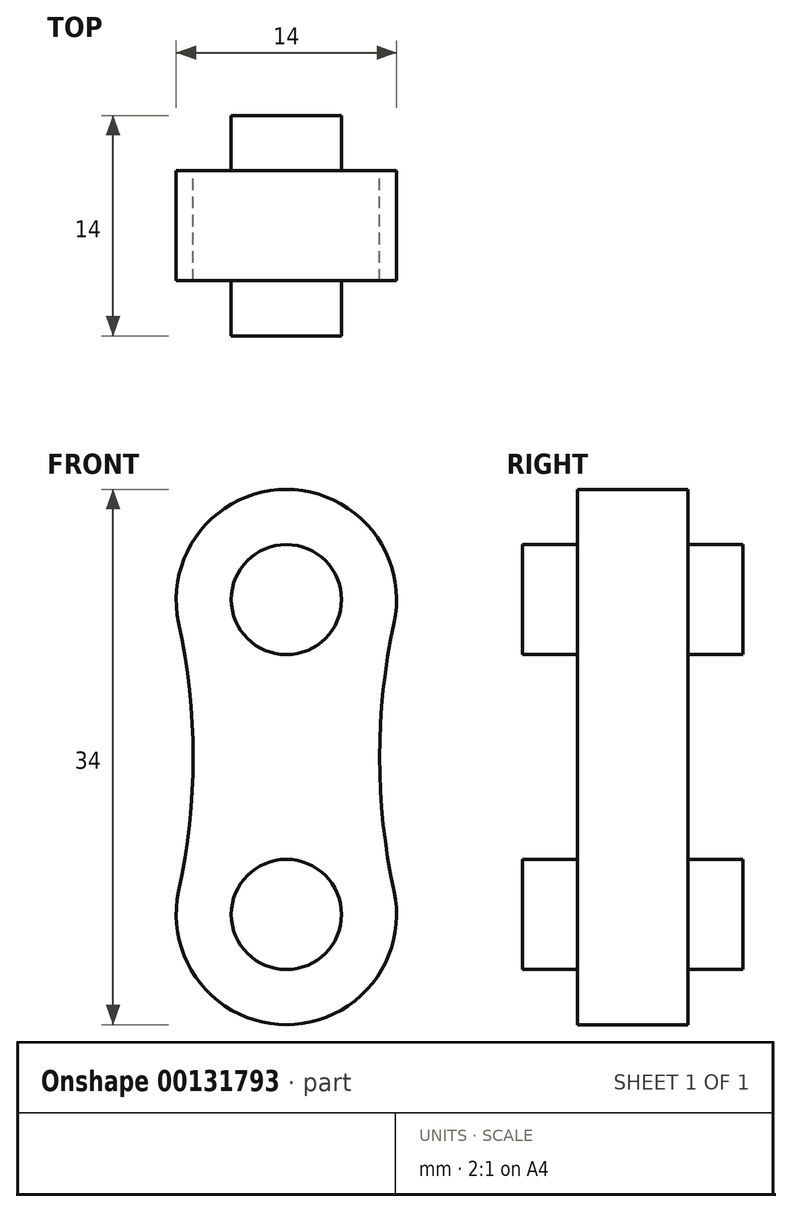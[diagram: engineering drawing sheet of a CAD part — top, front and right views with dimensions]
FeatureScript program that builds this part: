
annotation { "Feature Type Name" : "Feature", "Feature Type Description" : "" }
export const myFeature = defineFeature(function(context is Context, id is Id, definition is map)
    precondition{}
    {
        {
            var Q0;
            Q0=qCreatedBy(makeId("Front.planeOp"),FACE);
            var sketch = newSketch(context, id + "F0", { "sketchPlane" : qUnion([Q0])});
            skArc(sketch, "E0", {"start": v(6.84, -1.49) * mm, "mid": v(0, 7) * mm, "end": v(-6.84, -1.49) * mm});
            skArc(sketch, "E1", {"start": v(-6.84, -18.51) * mm, "mid": v(0, -27) * mm, "end": v(6.84, -18.51) * mm});
            skArc(sketch, "E2", {"start": v(-6.84, -18.51) * mm, "mid": v(-5.92, -10) * mm, "end": v(-6.84, -1.49) * mm});
            skArc(sketch, "E3", {"start": v(6.84, -1.49) * mm, "mid": v(5.92, -10) * mm, "end": v(6.84, -18.51) * mm});
            skSolve(sketch);
        }
        {
            var Q0;
            Q0=makeQuery(id+"F0.imprint","IMPRINT",FACE,{"disambiguationData":[TD([[makeQuery(id+"F0.imprint","IMPRINT",EDGE,{"derivedFrom":sQuery(id+"F0.wireOp",EDGE,"E0")}),1.0]])]});
            extrude(context, id + "F1", {"entities" : qUnion([Q0]), "depth" : 7 * mm});
        }
        {
            var Q0;
            Q0=makeQuery(id+"F1.opExtrude","CAP_FACE",FACE,{"disambiguationData":[OSD([sQuery(id+"F0.wireOp",EDGE,"E0"),sQuery(id+"F0.wireOp",EDGE,"E1"),sQuery(id+"F0.wireOp",EDGE,"E2"),sQuery(id+"F0.wireOp",EDGE,"E3")])],"isStart":false});
            var sketch = newSketch(context, id + "F2", { "sketchPlane" : qUnion([Q0])});
            skCircle(sketch, "E4", {"center": v(0, 0) * mm, "radius": 3.5 * mm});
            skCircle(sketch, "E5", {"center": v(0, -20) * mm, "radius": 3.5 * mm});
            skSolve(sketch);
        }
        {
            var Q0;
            Q0=makeQuery(id+"F2.imprint","IMPRINT",FACE,{"disambiguationData":[TD([[makeQuery(id+"F2.imprint","IMPRINT",EDGE,{"derivedFrom":sQuery(id+"F2.wireOp",EDGE,"E4")}),1.0]])]});
            var Q1;
            Q1=makeQuery(id+"F2.imprint","IMPRINT",FACE,{"disambiguationData":[TD([[makeQuery(id+"F2.imprint","IMPRINT",EDGE,{"derivedFrom":sQuery(id+"F2.wireOp",EDGE,"E5")}),1.0]])]});
            extrude(context, id + "F3", {"entities" : qUnion([Q0, Q1]), "operationType" : NewBodyOperationType.ADD, "depth" : 3.5 * mm});
        }
        {
            var Q0;
            Q0=makeQuery(id+"F1.opExtrude","CAP_FACE",FACE,{"disambiguationData":[OSD([sQuery(id+"F0.wireOp",EDGE,"E0"),sQuery(id+"F0.wireOp",EDGE,"E1"),sQuery(id+"F0.wireOp",EDGE,"E2"),sQuery(id+"F0.wireOp",EDGE,"E3")])],"isStart":true});
            var sketch = newSketch(context, id + "F4", { "sketchPlane" : qUnion([Q0])});
            skCircle(sketch, "E6", {"center": v(0, 0) * mm, "radius": 3.5 * mm});
            skCircle(sketch, "E7", {"center": v(0, -20) * mm, "radius": 3.5 * mm});
            skSolve(sketch);
        }
        {
            var Q0;
            Q0=makeQuery(id+"F4.imprint","IMPRINT",FACE,{"disambiguationData":[TD([[makeQuery(id+"F4.imprint","IMPRINT",EDGE,{"derivedFrom":sQuery(id+"F4.wireOp",EDGE,"E6")}),1.0]])]});
            var Q1;
            Q1=makeQuery(id+"F4.imprint","IMPRINT",FACE,{"disambiguationData":[TD([[makeQuery(id+"F4.imprint","IMPRINT",EDGE,{"derivedFrom":sQuery(id+"F4.wireOp",EDGE,"E7")}),1.0]])]});
            extrude(context, id + "F5", {"entities" : qUnion([Q0, Q1]), "operationType" : NewBodyOperationType.ADD, "depth" : 3.5 * mm});
        }
    });
